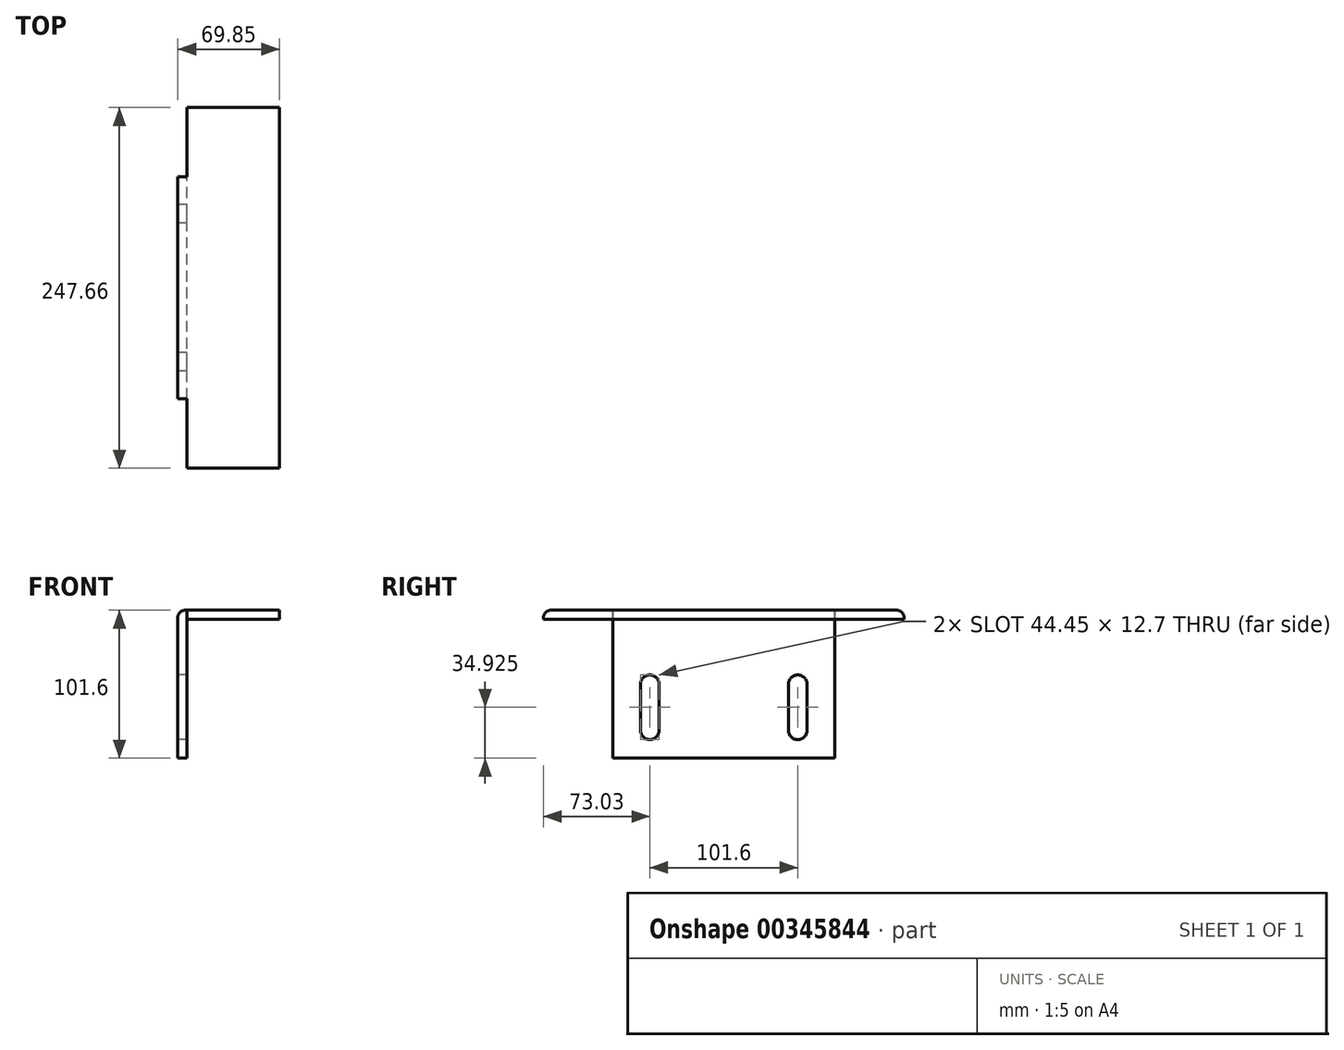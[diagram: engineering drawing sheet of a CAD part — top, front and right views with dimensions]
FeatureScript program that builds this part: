
annotation { "Feature Type Name" : "Feature", "Feature Type Description" : "" }
export const myFeature = defineFeature(function(context is Context, id is Id, definition is map)
    precondition{}
    {
        {
            var Q0;
            Q0=qCreatedBy(makeId("Front.planeOp"),FACE);
            var sketch = newSketch(context, id + "F6", { "sketchPlane" : qUnion([Q0])});
            skLineSegment(sketch, "E0.bottom", {"start": v(6.35, -25.4) * mm, "end": v(-6.35, -25.4) * mm});
            skLineSegment(sketch, "E0.top", {"start": v(6.35, 25.4) * mm, "end": v(-6.35, 25.4) * mm});
            skLineSegment(sketch, "E0.left", {"start": v(6.35, -25.4) * mm, "end": v(6.35, 25.4) * mm});
            skLineSegment(sketch, "E0.right", {"start": v(-6.35, -25.4) * mm, "end": v(-6.35, 25.4) * mm});
            skPoint(sketch, "E0.middle", {"position": v(0, 0) * mm});
            skLineSegment(sketch, "E1.bottom", {"start": v(6.35, 25.4) * mm, "end": v(69.85, 25.4) * mm});
            skLineSegment(sketch, "E1.top", {"start": v(6.35, 19.05) * mm, "end": v(69.85, 19.05) * mm});
            skLineSegment(sketch, "E1.left", {"start": v(6.35, 25.4) * mm, "end": v(6.35, 19.05) * mm});
            skLineSegment(sketch, "E1.right", {"start": v(69.85, 25.4) * mm, "end": v(69.85, 19.05) * mm});
            skSolve(sketch);
        }
        {
            var Q0;
            Q0=makeQuery(id+"F6.imprint","IMPRINT",FACE,{"disambiguationData":[TD([[makeQuery(id+"F6.imprint","IMPRINT",EDGE,{"derivedFrom":sQuery(id+"F6.wireOp",EDGE,"E1.bottom")}),-1.0]])]});
            extrude(context, id + "F0", {"entities" : qUnion([Q0]), "depth" : 123.82 * mm});
        }
        {
            var Q0;
            Q0=makeQuery(id+"F0.opExtrude","SWEPT_BODY",BODY,{"disambiguationData":[OSD([sQuery(id+"F6.wireOp",EDGE,"E1.bottom"),sQuery(id+"F6.wireOp",EDGE,"E1.top"),sQuery(id+"F6.wireOp",EDGE,"E1.left"),sQuery(id+"F6.wireOp",EDGE,"E1.right")])]});
            var Q1;
            Q1=qCreatedBy(makeId("Front.planeOp"),FACE);
            mirror(context, id + "F1", {"operationType" : NewBodyOperationType.ADD, "entities" : qUnion([Q0]), "mirrorPlane" : qUnion([Q1])});
        }
        {
            var Q0;
            Q0=makeQuery(id+"F0.opExtrude","SWEPT_BODY",BODY,{"disambiguationData":[OSD([sQuery(id+"F6.wireOp",EDGE,"E1.bottom"),sQuery(id+"F6.wireOp",EDGE,"E1.top"),sQuery(id+"F6.wireOp",EDGE,"E1.left"),sQuery(id+"F6.wireOp",EDGE,"E1.right")])]});
            var Q1;
            Q1=qCreatedBy(makeId("Front.planeOp"),FACE);
            mirror(context, id + "F2", {"operationType" : NewBodyOperationType.ADD, "entities" : qUnion([Q0]), "mirrorPlane" : qUnion([Q1])});
        }
        {
            var Q0;
            Q0=qCreatedBy(makeId("Right.planeOp"),FACE);
            var sketch = newSketch(context, id + "F3", { "sketchPlane" : qUnion([Q0])});
            skLineSegment(sketch, "E2.bottom", {"start": v(76.2, 25.4) * mm, "end": v(-76.2, 25.4) * mm});
            skLineSegment(sketch, "E2.top", {"start": v(76.2, -76.2) * mm, "end": v(-76.2, -76.2) * mm});
            skLineSegment(sketch, "E2.left", {"start": v(76.2, 25.4) * mm, "end": v(76.2, -76.2) * mm});
            skLineSegment(sketch, "E2.right", {"start": v(-76.2, 25.4) * mm, "end": v(-76.2, -76.2) * mm});
            skLineSegment(sketch, "E3.bottom", {"start": v(-50.8, -63.5) * mm, "end": v(-50.8, -63.5) * mm});
            skLineSegment(sketch, "E3.top", {"start": v(-50.8, 12.7) * mm, "end": v(-50.8, 12.7) * mm});
            skLineSegment(sketch, "E3.left", {"start": v(-57.15, -57.15) * mm, "end": v(-57.15, -25.4) * mm});
            skLineSegment(sketch, "E3.right", {"start": v(-44.45, -57.15) * mm, "end": v(-44.45, -25.4) * mm});
            skPoint(sketch, "E3.middle", {"position": v(-50.8, -25.4) * mm});
            skLineSegment(sketch, "E4.bottom", {"start": v(50.8, -63.5) * mm, "end": v(50.8, -63.5) * mm});
            skLineSegment(sketch, "E4.top", {"start": v(50.8, 12.7) * mm, "end": v(50.8, 12.7) * mm});
            skLineSegment(sketch, "E4.left", {"start": v(44.45, -57.15) * mm, "end": v(44.45, -25.4) * mm});
            skLineSegment(sketch, "E4.right", {"start": v(57.15, -57.15) * mm, "end": v(57.15, -25.4) * mm});
            skPoint(sketch, "E4.middle", {"position": v(50.8, -25.4) * mm});
            skPoint(sketch, "E5.visualSharp", {"position": v(57.15, 12.7) * mm});
            skPoint(sketch, "E6.visualSharp", {"position": v(57.15, -63.5) * mm});
            skArc(sketch, "E6.filletArc", {"start": v(50.8, -63.5) * mm, "mid": v(55.3, -61.64) * mm, "end": v(57.15, -57.15) * mm});
            skPoint(sketch, "E7.visualSharp", {"position": v(44.45, -63.5) * mm});
            skArc(sketch, "E7.filletArc", {"start": v(44.45, -57.15) * mm, "mid": v(46.3, -61.64) * mm, "end": v(50.8, -63.5) * mm});
            skPoint(sketch, "E8.visualSharp", {"position": v(44.45, 12.7) * mm});
            skPoint(sketch, "E9.visualSharp", {"position": v(-57.15, 12.7) * mm});
            skPoint(sketch, "E10.visualSharp", {"position": v(-44.45, 12.7) * mm});
            skPoint(sketch, "E11.visualSharp", {"position": v(-44.45, -63.5) * mm});
            skArc(sketch, "E11.filletArc", {"start": v(-50.8, -63.5) * mm, "mid": v(-46.3, -61.64) * mm, "end": v(-44.45, -57.15) * mm});
            skPoint(sketch, "E12.visualSharp", {"position": v(-57.15, -63.5) * mm});
            skArc(sketch, "E12.filletArc", {"start": v(-57.15, -57.15) * mm, "mid": v(-55.3, -61.64) * mm, "end": v(-50.8, -63.5) * mm});
            skArc(sketch, "E13", {"start": v(-44.45, -25.4) * mm, "mid": v(-50.8, -19.05) * mm, "end": v(-57.15, -25.4) * mm});
            skArc(sketch, "E14", {"start": v(57.15, -25.4) * mm, "mid": v(50.8, -19.05) * mm, "end": v(44.45, -25.4) * mm});
            skSolve(sketch);
        }
        {
            var Q0;
            Q0=makeQuery(id+"F3.imprint","IMPRINT",FACE,{"disambiguationData":[TD([[makeQuery(id+"F3.imprint","IMPRINT",EDGE,{"derivedFrom":sQuery(id+"F3.wireOp",EDGE,"E2.bottom")}),1.0]])]});
            extrude(context, id + "F4", {"entities" : qUnion([Q0]), "operationType" : NewBodyOperationType.ADD, "depth" : 6.35 * mm});
        }
        {
            var Q0;
            Q0=makeQuery(id+"F4.opExtrude","CAP_EDGE",EDGE,{"disambiguationData":[OSD([sQuery(id+"F3.wireOp",EDGE,"E2.bottom")])],"isStart":true});
            var Q1;
            Q1=makeQuery(id+"F1.opPattern","COPY",EDGE,{"derivedFrom":makeQuery(id+"F0.opExtrude","CAP_EDGE",EDGE,{"disambiguationData":[OSD([sQuery(id+"F6.wireOp",EDGE,"E1.bottom")])],"isStart":false}),"instanceName":"1"});
            var Q2;
            Q2=makeQuery(id+"F0.opExtrude","CAP_EDGE",EDGE,{"disambiguationData":[OSD([sQuery(id+"F6.wireOp",EDGE,"E1.bottom")])],"isStart":false});
            fillet(context, id + "F5", {"entities" : qUnion([Q0, Q1, Q2]), "radius" : 5.08 * mm, "tangentPropagation" : true, "allowEdgeOverflow" : false});
        }
    });
